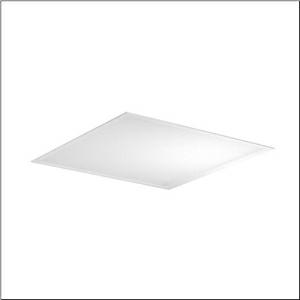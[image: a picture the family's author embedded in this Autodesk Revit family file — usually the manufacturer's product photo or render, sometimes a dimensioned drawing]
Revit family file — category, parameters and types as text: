
# Revit family: apollon_21_square_51mq12wd2t13
name_source: partatom
category: Lighting Fixtures
units: mm (PartAtom-declared; Revit-internal decimal feet)

## family parameters
Cut with Voids When Loaded = No
Host = Face
Light Source = No
Part Type = Normal
Room Calculation Point = No
Round Connector Dimension = Use Diameter
Shared = No

## types (1)
- --- (1 x LED 2700 K ... 6500 K, 4000 lm, 40 W, 2700K)
    Apparent Load = 40 VA
    CIE Flux Codes = 61 87 97 100 100
    Color Rendering = 80
    Color Temperature = 2700K
    Default Elevation = 1800 mm
    Description = Apollon 21 square, office luminaire, primary optical cover: micro prismatic cover, of PMMA, CAT 2 (L<= 3000cd/m²), light emission: direct distribution, primary light characteristic: symmetric, installation type: lay-in mounting, recessed, LED, rated luminous flux: 4.000lm, luminous efficacy: 100lm/W, light colour: 8tw, colour temperature: 2700..6500K, control gear: DALI-2 DT8, with terminal, 5-pole, mains connection: 220..240V, AC, 50/60Hz, rated input power: 40W, housing, of aluminium, traffic white (RAL 9016), module: M600, length: 596mm, width: 596mm, height: 40mm, housing upper side, of sheet steel, galvanised, protection rating (complete): IP20, protection rating (lamp compartment, on room side): IP50, insulation class (complete): insulation class I (protective earthing), certification: CE, ENEC, permissible operating ambient temperature: -20..+40°C, packaging unit: 1 piece
    Height = 0 mm  [stored 0 ft]
    Lamp = 1 x LED 2700 K ... 6500 K
    Lamp Light Flux = 4000 lm
    Lamp Power = 40 W
    Lamp count = 1
    Length = 595 mm
    Luminous efficacy = 100 lm/W
    Manufacturer = Siteco
    ModVariant = No
    Model = 51MQ12WD2T13
    Mounting Place = Ceiling
    Mounting Type = Recessed
    Number of Poles = 1
    OnlyDefault = Yes
    Power Factor = 1
    Product Name = Apollon 21 square
    Product group = office luminaire | ceiling recessed
    ProductGroupID = 400
    Protection Class = Protection class I
    Protection Degree = IP 20
    RLX_Detail_Level = 1
    RLX_Emergency_Light_Flux = 0 lm
    RLX_Emergency_Type = 0
    RLX_Emergency_Type_DB = No
    RlxData = <blob elided: 12657 chars, md5=c782ae57>
    Socket = socket
    Standby Power = 0 W
    System Light Flux = 4000 lm
    System Power = 40 W
    Type Comments = individual setting: CCT=2700K
    Type Image = l_1291049.jpg
    URL = http://relux.com
    VarID = @adj_103019
    Voltage = 0 V
    Weight = 0.00 kg
    Width = 595 mm

note: [stored X ft] marks values corroborated as IEEE doubles in the binary element streams (Revit-internal decimal feet)

## geometry (parser evidence)
native form markers: Sweep x8
no freeform markers — native parametric forms only
